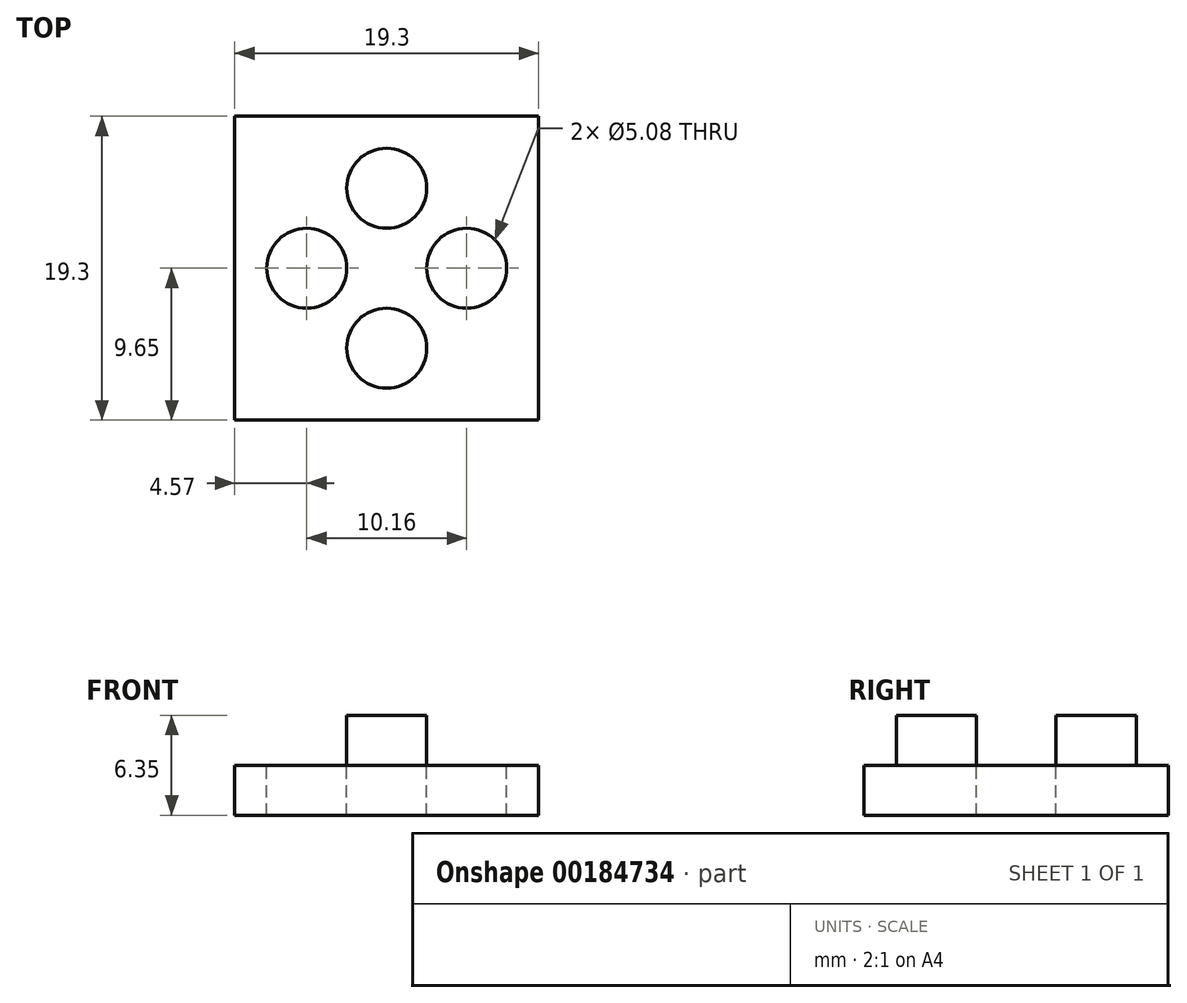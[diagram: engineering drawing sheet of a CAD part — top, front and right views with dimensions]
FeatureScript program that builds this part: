
annotation { "Feature Type Name" : "Feature", "Feature Type Description" : "" }
export const myFeature = defineFeature(function(context is Context, id is Id, definition is map)
    precondition{}
    {
        {
            var Q0;
            Q0=qCreatedBy(makeId("Top.planeOp"),FACE);
            var sketch = newSketch(context, id + "F0", { "sketchPlane" : qUnion([Q0])});
            skLineSegment(sketch, "E0.bottom", {"start": v(9.65, -9.65) * mm, "end": v(-9.65, -9.65) * mm});
            skLineSegment(sketch, "E0.top", {"start": v(9.65, 9.65) * mm, "end": v(-9.65, 9.65) * mm});
            skLineSegment(sketch, "E0.left", {"start": v(9.65, -9.65) * mm, "end": v(9.65, 9.65) * mm});
            skLineSegment(sketch, "E0.right", {"start": v(-9.65, -9.65) * mm, "end": v(-9.65, 9.65) * mm});
            skPoint(sketch, "E0.middle", {"position": v(0, 0) * mm});
            skSolve(sketch);
        }
        {
            var Q0;
            Q0 = qSketchRegion(id + "F0", true);
            extrude(context, id + "F1", {"entities" : qUnion([Q0]), "depth" : 6.35 * mm});
        }
        {
            var Q0;
            Q0=makeQuery(id+"F1.opExtrude","CAP_FACE",FACE,{"disambiguationData":[OSD([sQuery(id+"F0.wireOp",EDGE,"E0.bottom"),sQuery(id+"F0.wireOp",EDGE,"E0.top"),sQuery(id+"F0.wireOp",EDGE,"E0.left"),sQuery(id+"F0.wireOp",EDGE,"E0.right")])],"isStart":false});
            var sketch = newSketch(context, id + "F2", { "sketchPlane" : qUnion([Q0])});
            skCircle(sketch, "E1", {"center": v(0, 5.08) * mm, "radius": 2.54 * mm});
            skCircle(sketch, "E2", {"center": v(0, -5.08) * mm, "radius": 2.54 * mm});
            skLineSegment(sketch, "E3.bottom", {"start": v(9.65, -9.65) * mm, "end": v(-9.65, -9.65) * mm});
            skLineSegment(sketch, "E3.top", {"start": v(9.65, 9.65) * mm, "end": v(-9.65, 9.65) * mm});
            skLineSegment(sketch, "E3.left", {"start": v(9.65, -9.65) * mm, "end": v(9.65, 9.65) * mm});
            skLineSegment(sketch, "E3.right", {"start": v(-9.65, -9.65) * mm, "end": v(-9.65, 9.65) * mm});
            skPoint(sketch, "E3.middle", {"position": v(0, 0) * mm});
            skSolve(sketch);
        }
        {
            var Q0;
            Q0 = qSketchRegion(id + "F2", true);
            extrude(context, id + "F3", {"entities" : qUnion([Q0]), "operationType" : NewBodyOperationType.REMOVE, "oppositeDirection" : true, "depth" : 3.17 * mm});
        }
        {
            var Q0;
            Q0=makeQuery(id+"F3.boolean.opBoolean","COPY",FACE,{"derivedFrom":makeQuery(id+"F3.opExtrude","CAP_FACE",FACE,{"disambiguationData":[OSD([sQuery(id+"F2.wireOp",EDGE,"E1"),sQuery(id+"F2.wireOp",EDGE,"E2"),sQuery(id+"F2.wireOp",EDGE,"E3.bottom"),sQuery(id+"F2.wireOp",EDGE,"E3.top"),sQuery(id+"F2.wireOp",EDGE,"E3.left"),sQuery(id+"F2.wireOp",EDGE,"E3.right")])],"isStart":false})});
            var sketch = newSketch(context, id + "F4", { "sketchPlane" : qUnion([Q0])});
            skCircle(sketch, "E4", {"center": v(5.08, 0) * mm, "radius": 2.54 * mm});
            skCircle(sketch, "E5", {"center": v(-5.08, 0) * mm, "radius": 2.54 * mm});
            skSolve(sketch);
        }
        {
            var Q0;
            Q0 = qSketchRegion(id + "F4", true);
            extrude(context, id + "F5", {"entities" : qUnion([Q0]), "operationType" : NewBodyOperationType.REMOVE, "oppositeDirection" : true, "depth" : 3.17 * mm});
        }
    });
